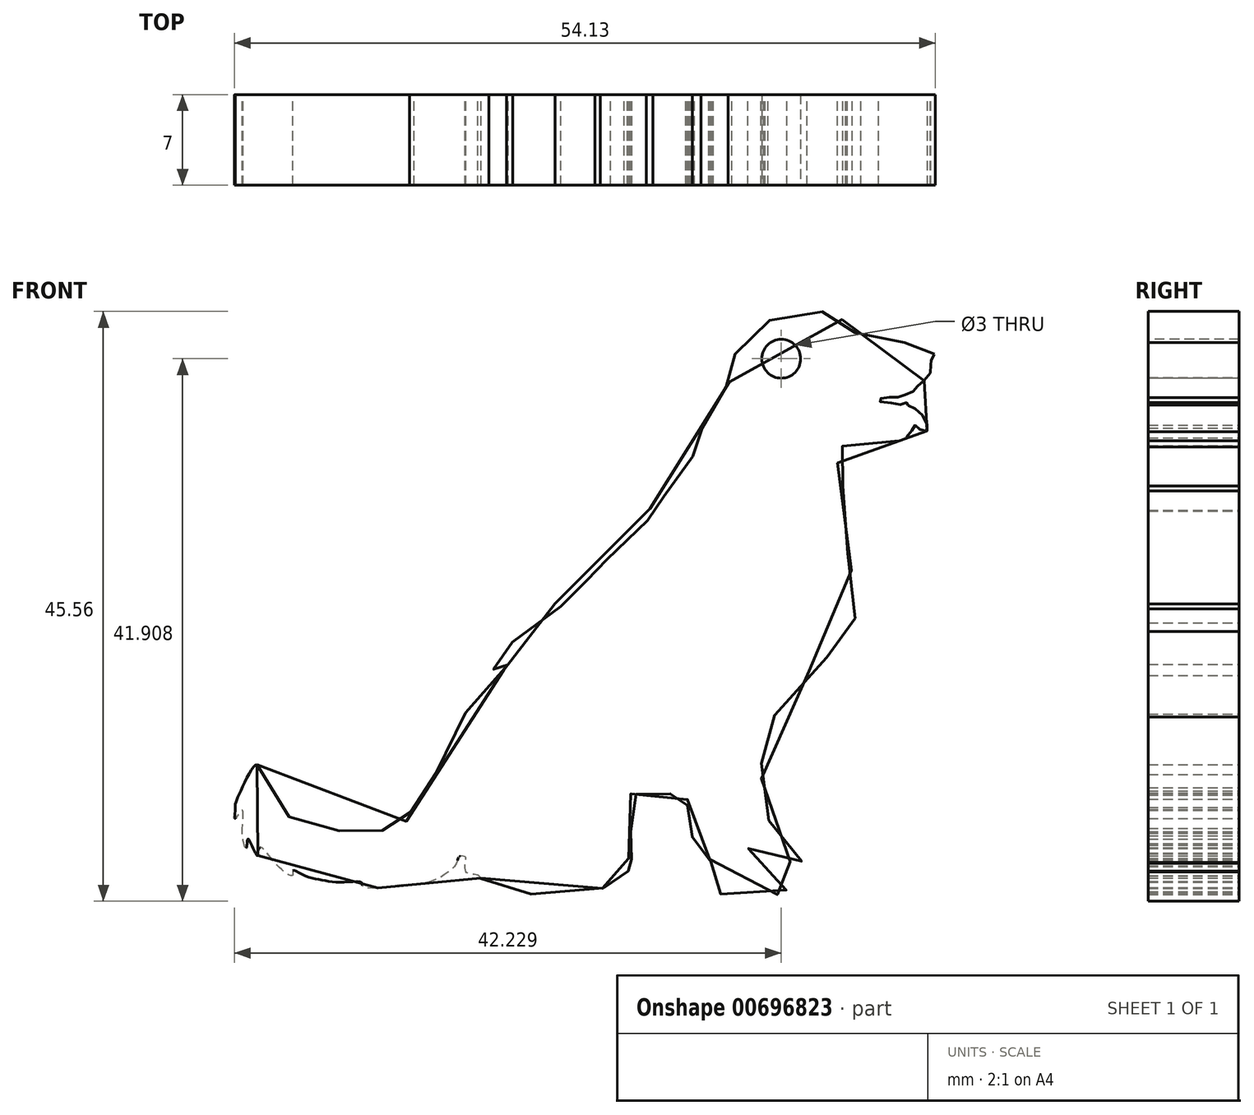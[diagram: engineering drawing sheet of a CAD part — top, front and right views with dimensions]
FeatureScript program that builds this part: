
annotation { "Feature Type Name" : "Feature", "Feature Type Description" : "" }
export const myFeature = defineFeature(function(context is Context, id is Id, definition is map)
    precondition{}
    {
        {
            var Q0;
            Q0=qCreatedBy(makeId("Front.planeOp"),FACE);
            var sketch = newSketch(context, id + "F0", { "sketchPlane" : qUnion([Q0])});
            skFitSpline(sketch, "E0", {"points": [v(-39.4, 16.74) * mm, v(-38.59, 14.62) * mm, v(-36.85, 12.67) * mm, v(-34.52, 11.86) * mm, v(-33.1, 11.53) * mm, v(-33, 11.8) * mm, v(-32.08, 11.37) * mm, v(-30.23, 11.48) * mm, v(-27.96, 12.34) * mm, v(-27.3, 12.67) * mm, v(-27.63, 12.94) * mm, v(-27.03, 13.43) * mm, v(-26.44, 14.57) * mm, v(-25.68, 15.92) * mm, v(-24.76, 18.7) * mm, v(-23.02, 21.08) * mm, v(-21.07, 23.25) * mm, v(-20.04, 24.5) * mm, v(-20.9, 23.95) * mm, v(-21.28, 23.8) * mm, v(-21.5, 23.63) * mm, v(-20.42, 24.93) * mm, v(-19.71, 25.8) * mm, v(-20.14, 25.85) * mm, v(-19.33, 26.4) * mm, v(-17.6, 27.59) * mm, v(-15.97, 29.05) * mm, v(-16.4, 29.22) * mm, v(-15.2, 30.03) * mm, v(-13.42, 31.44) * mm, v(-12.93, 31.98) * mm, v(-13.3, 32.04) * mm, v(-12.55, 32.47) * mm, v(-11.2, 33.83) * mm, v(-9.73, 35.13) * mm, v(-8.86, 36.38) * mm, v(-9.35, 36.32) * mm, v(-8.37, 37.03) * mm, v(-7.18, 38.7) * mm, v(-5.64, 40.14) * mm, v(-5.79, 40.7) * mm, v(-4.82, 41.57) * mm, v(-4.46, 42.7) * mm, v(-5.12, 42.75) * mm, v(-4.3, 43.57) * mm, v(-3.48, 45.41) * mm, v(-2.77, 46.64) * mm, v(-2.97, 46.64) * mm, v(-2.87, 47.66) * mm, v(-2.15, 48.94) * mm, v(-0.62, 50.43) * mm, v(0, 51) * mm, v(1.2, 51.36) * mm, v(3.52, 51.63) * mm, v(4.75, 51.72) * mm, v(5.71, 51.17) * mm, v(6.35, 50.54) * mm, v(7.3, 49.67) * mm, v(8.77, 49.3) * mm, v(10.86, 49.3) * mm, v(11.82, 48.99) * mm, v(12.88, 48.87) * mm, v(12.96, 48.58) * mm, v(12.76, 48.22) * mm, v(12.6, 47.75) * mm, v(12.61, 47.63) * mm, v(12.5, 46.82) * mm, v(11.7, 46.1) * mm, v(11.31, 45.64) * mm, v(10.58, 45.27) * mm, v(9.9, 45.1) * mm, v(8.94, 45.1) * mm, v(8.6, 44.85) * mm, v(9.73, 44.66) * mm, v(10.5, 44.56) * mm, v(10.83, 44.72) * mm, v(10.89, 44.5) * mm, v(11.54, 44.18) * mm, v(12.27, 43.18) * mm, v(12.3, 42.5) * mm, v(11.76, 42.65) * mm, v(11.42, 42.96) * mm, v(11.17, 42.6) * mm, v(10.68, 42) * mm, v(10.01, 41.76) * mm, v(9.06, 41.86) * mm, v(8.12, 41.9) * mm, v(7.2, 41.92) * mm, v(7.13, 41.6) * mm, v(6.3, 41.29) * mm, v(5.79, 41.35) * mm, v(5.48, 40.6) * mm, v(5.52, 39.58) * mm, v(6, 39.03) * mm, v(6.17, 38.28) * mm, v(6.13, 37.88) * mm, v(5.93, 38.1) * mm, v(5.83, 38.28) * mm, v(5.9, 37.49) * mm, v(6.1, 35.94) * mm, v(6.54, 34.56) * mm, v(6.1, 34.23) * mm, v(6.18, 33.22) * mm, v(6.34, 32.28) * mm, v(6.9, 30.41) * mm, v(7.2, 28.79) * mm, v(6.9, 29.15) * mm, v(6.79, 28.22) * mm, v(6.58, 27.04) * mm, v(6.3, 27.32) * mm, v(6.18, 27.69) * mm, v(5.93, 26.55) * mm, v(5.65, 25.74) * mm, v(4.3, 24.85) * mm, v(2.76, 23.5) * mm, v(1.75, 22) * mm, v(1.1, 20.42) * mm, v(0.7, 20.66) * mm, v(0.37, 20.05) * mm, v(0.16, 19.67) * mm, v(-0.16, 18.95) * mm, v(-0.2, 18.4) * mm, v(-0.3, 17.92) * mm, v(-0.2, 17.25) * mm, v(-0.4, 17.1) * mm, v(-0.47, 16.3) * mm, v(-0.47, 15.22) * mm, v(-0.27, 14.5) * mm, v(0, 13.52) * mm, v(-0.49, 13.35) * mm, v(0, 12.74) * mm, v(0.27, 11.58) * mm, v(1.26, 11.34) * mm, v(1.97, 11.03) * mm, v(2.93, 10.41) * mm, v(3, 9.77) * mm, v(2.52, 9.22) * mm, v(1.53, 9.25) * mm, v(0.68, 9.12) * mm, v(-0.32, 9.32) * mm, v(-0.86, 9.5) * mm, v(-1.1, 9.42) * mm, v(-1.48, 10.28) * mm, v(-1.37, 9.46) * mm, v(-0.66, 8.88) * mm, v(0.47, 8.47) * mm, v(0.78, 8.5) * mm, v(1.43, 7.75) * mm, v(1.36, 6.93) * mm, v(0.33, 6.59) * mm, v(-0.45, 6.25) * mm, v(-1.68, 6.28) * mm, v(-2.37, 6.52) * mm, v(-3.53, 6.72) * mm, v(-4.21, 7.3) * mm, v(-4.18, 8.13) * mm, v(-4.32, 7.98) * mm, v(-4.38, 8.08) * mm, v(-4.4, 8.28) * mm, v(-4.3, 8.42) * mm, v(-4.22, 8.94) * mm, v(-4.4, 8.86) * mm, v(-4.37, 9.14) * mm, v(-4.39, 9.43) * mm, v(-4.48, 9.43) * mm, v(-4.5, 9.72) * mm, v(-4.52, 9.9) * mm, v(-5.07, 9.92) * mm, v(-5.18, 10.63) * mm, v(-6.06, 10.51) * mm, v(-5.9, 10.83) * mm, v(-5.78, 11.24) * mm, v(-5.8, 11.56) * mm, v(-6.14, 11.45) * mm, v(-5.98, 11.8) * mm, v(-6.02, 12.43) * mm, v(-5.95, 13.04) * mm, v(-6, 13.43) * mm, v(-6.28, 13.3) * mm, v(-6.18, 13.58) * mm, v(-6.18, 14.26) * mm, v(-6.17, 14.96) * mm, v(-6.33, 15.5) * mm, v(-6.37, 16) * mm, v(-6.73, 15.5) * mm, v(-7.24, 14.79) * mm, v(-7.68, 14.25) * mm, v(-7.8, 14.07) * mm, v(-7.92, 14.94) * mm, v(-8.37, 14.61) * mm, v(-8.84, 14.64) * mm, v(-9.25, 14.7) * mm, v(-9.5, 14.42) * mm, v(-10.06, 14.45) * mm, v(-10.86, 14.4) * mm, v(-11.07, 13.92) * mm, v(-10.73, 13.4) * mm, v(-10.48, 13) * mm, v(-10.46, 12.63) * mm, v(-10.52, 12.24) * mm, v(-10.55, 11.86) * mm, v(-10.5, 11.41) * mm, v(-10.05, 11.1) * mm, v(-9.76, 10.98) * mm, v(-9.6, 10.72) * mm, v(-9.41, 10.42) * mm, v(-9.44, 9.87) * mm, v(-9.63, 9.43) * mm, v(-10.25, 9.38) * mm, v(-10.75, 9.51) * mm, v(-11.1, 9.57) * mm, v(-11.55, 9.69) * mm, v(-11.87, 9.68) * mm, v(-12.11, 9.6) * mm, v(-11.47, 9.35) * mm, v(-11.07, 9.01) * mm, v(-10.86, 8.74) * mm, v(-10.71, 8.39) * mm, v(-10.71, 8.12) * mm, v(-10.8, 7.93) * mm, v(-10.8, 7.5) * mm, v(-10.84, 7.26) * mm, v(-11.12, 6.96) * mm, v(-11.76, 6.87) * mm, v(-12.27, 6.9) * mm, v(-12.63, 7.23) * mm, v(-13, 6.98) * mm, v(-14, 6.94) * mm, v(-15.08, 6.9) * mm, v(-16.84, 6.73) * mm, v(-17.9, 6.75) * mm, v(-19.1, 6.7) * mm, v(-19.49, 6.73) * mm, v(-21.37, 6.82) * mm, v(-22.17, 6.96) * mm, v(-22.35, 7.57) * mm, v(-22.13, 7.82) * mm, v(-22.33, 8.19) * mm, v(-22.9, 8.28) * mm, v(-23.27, 8.47) * mm, v(-23.34, 9.2) * mm, v(-23.32, 9.6) * mm, v(-23.8, 9.64) * mm, v(-23.98, 9.18) * mm, v(-24.7, 8.42) * mm, v(-25.62, 7.86) * mm, v(-26.9, 7.53) * mm, v(-28.1, 7.46) * mm, v(-30.02, 7.2) * mm, v(-31.28, 7.36) * mm, v(-31.34, 7.63) * mm, v(-32.86, 7.67) * mm, v(-34.49, 7.84) * mm, v(-35.85, 8.22) * mm, v(-36.63, 8.55) * mm, v(-36.67, 8.2) * mm, v(-37.8, 8.9) * mm, v(-39.15, 10.33) * mm, v(-39.35, 10) * mm, v(-39.39, 9.7) * mm, v(-39.9, 10.64) * mm, v(-40.13, 11) * mm, v(-40.26, 10.32) * mm, v(-40.55, 11.41) * mm, v(-40.58, 13.22) * mm, v(-41.13, 12.57) * mm, v(-41.11, 13) * mm, v(-41.1, 13.43) * mm, v(-41.09, 13.71) * mm, v(-40.53, 15.04) * mm, v(-39.4, 16.74) * mm]});
            skSolve(sketch);
        }
        {
            var Q0;
            Q0=makeQuery(id+"F0.imprint","IMPRINT",FACE,{"disambiguationData":[TD([[makeQuery(id+"F0.imprint","IMPRINT",EDGE,{"derivedFrom":sQuery(id+"F0.wireOp",EDGE,"E0")}),-1.0]])]});
            extrude(context, id + "F1", {"entities" : qUnion([Q0]), "depth" : 7 * mm, "offsetDistance" : 25.4 * mm});
        }
        {
            var Q0;
            Q0=makeQuery(id+"F1.opExtrude","CAP_FACE",FACE,{"disambiguationData":[OSD([sQuery(id+"F0.wireOp",EDGE,"E0")])],"isStart":false});
            var sketch = newSketch(context, id + "F2", { "sketchPlane" : qUnion([Q0])});
            skCircle(sketch, "E1", {"center": v(1.07, 48.1) * mm, "radius": 1.55 * mm});
            skSolve(sketch);
        }
        {
            var Q0;
            Q0=sQuery(id+"F2.wireOp",VERTEX,"E1.center");
            var Q1;
            Q1=makeQuery(id+"F1.opExtrude","SWEPT_BODY",BODY,{"disambiguationData":[OSD([sQuery(id+"F0.wireOp",EDGE,"E0")])]});
            hole(context, id + "F3", {"style" : HoleStyle.SIMPLE, "endStyle" : HoleEndStyle.THROUGH, "holeDiameter" : 3 * mm, "majorDiameter" : 6.35 * mm, "isTappedThrough" : true, "tappedDepth" : 12.7 * mm, "tapClearance" : 3, "locations" : qUnion([Q0]), "scope" : qUnion([Q1])});
        }
    });
